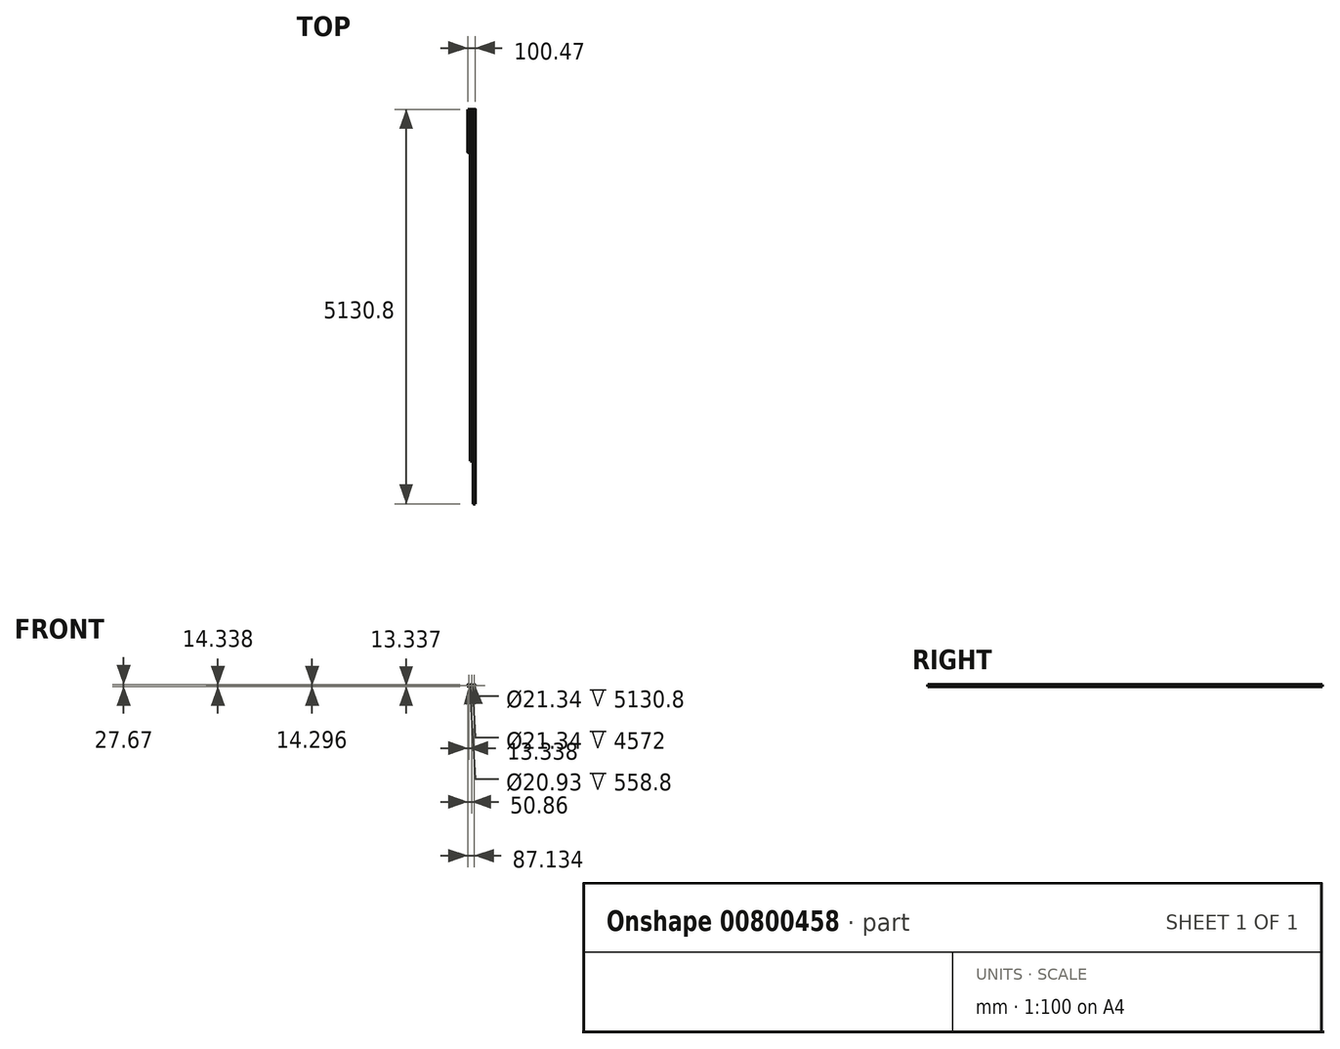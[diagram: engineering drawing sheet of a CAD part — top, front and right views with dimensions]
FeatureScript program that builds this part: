
annotation { "Feature Type Name" : "Feature", "Feature Type Description" : "" }
export const myFeature = defineFeature(function(context is Context, id is Id, definition is map)
    precondition{}
    {
        {
            var Q0;
            Q0=qCreatedBy(makeId("Front.planeOp"),FACE);
            var sketch = newSketch(context, id + "F0", { "sketchPlane" : qUnion([Q0])});
            skCircle(sketch, "E0", {"center": v(-57.1, 47.72) * mm, "radius": 13.34 * mm});
            skCircle(sketch, "E1", {"center": v(-57.1, 47.72) * mm, "radius": 10.46 * mm});
            skSolve(sketch);
        }
        {
            var Q0;
            Q0 = qSketchRegion(id + "F0", true);
            extrude(context, id + "F1", {"entities" : qUnion([Q0]), "depth" : 558.8 * mm, "offsetDistance" : 25.4 * mm});
        }
        {
            var Q0;
            Q0=qCreatedBy(makeId("Front.planeOp"),FACE);
            var sketch = newSketch(context, id + "F2", { "sketchPlane" : qUnion([Q0])});
            skCircle(sketch, "E2", {"center": v(-19.57, 47.76) * mm, "radius": 10.67 * mm});
            skCircle(sketch, "E3", {"center": v(-19.57, 47.76) * mm, "radius": 13.34 * mm});
            skSolve(sketch);
        }
        {
            var Q0;
            Q0 = qSketchRegion(id + "F2", true);
            extrude(context, id + "F3", {"entities" : qUnion([Q0]), "depth" : 4572 * mm, "offsetDistance" : 25.4 * mm});
        }
        {
            var Q0;
            Q0=qCreatedBy(makeId("Front.planeOp"),FACE);
            var sketch = newSketch(context, id + "F4", { "sketchPlane" : qUnion([Q0])});
            skCircle(sketch, "E4", {"center": v(16.7, 46.76) * mm, "radius": 10.67 * mm});
            skCircle(sketch, "E5", {"center": v(16.7, 46.76) * mm, "radius": 13.34 * mm});
            skSolve(sketch);
        }
        {
            var Q0;
            Q0 = qSketchRegion(id + "F4", true);
            extrude(context, id + "F5", {"entities" : qUnion([Q0]), "depth" : 5130.8 * mm, "offsetDistance" : 25.4 * mm});
        }
    });
